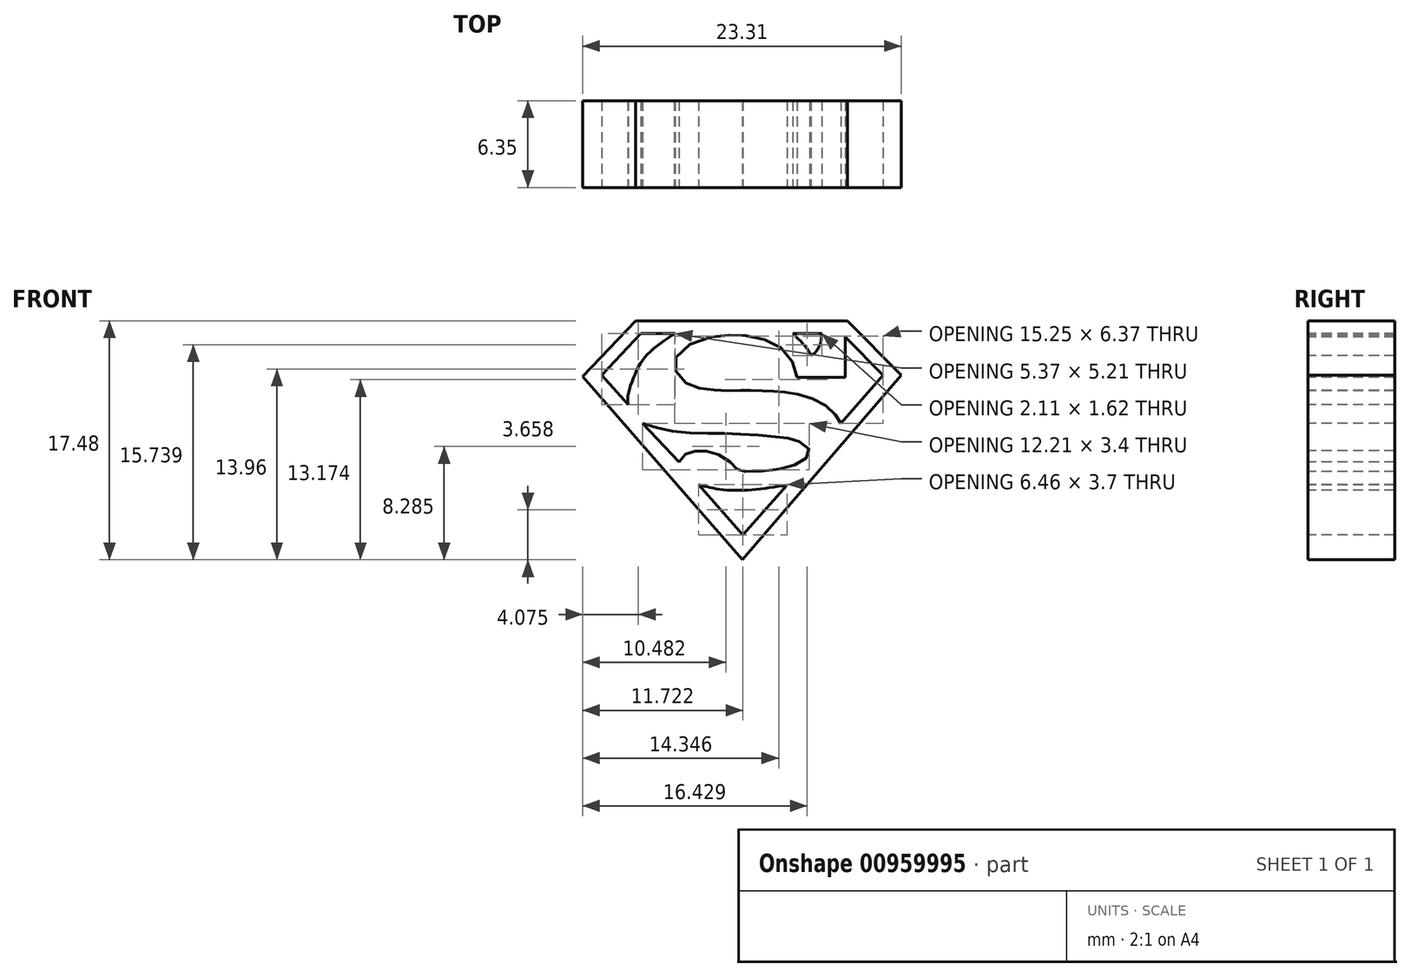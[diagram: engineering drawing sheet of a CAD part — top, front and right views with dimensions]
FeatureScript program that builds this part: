
annotation { "Feature Type Name" : "Feature", "Feature Type Description" : "" }
export const myFeature = defineFeature(function(context is Context, id is Id, definition is map)
    precondition{}
    {
        {
            var Q0;
            Q0=qCreatedBy(makeId("Front.planeOp"),FACE);
            var sketch = newSketch(context, id + "F0", { "sketchPlane" : qUnion([Q0])});
            skLineSegment(sketch, "E0", {"start": v(0, 0) * mm, "end": v(0, 25.4) * mm});
            skLineSegment(sketch, "E1", {"start": v(0, 25.4) * mm, "end": v(25.4, 25.4) * mm});
            skLineSegment(sketch, "E2", {"start": v(25.4, 25.4) * mm, "end": v(25.4, 0) * mm});
            skLineSegment(sketch, "E3", {"start": v(25.4, 0) * mm, "end": v(0, 0) * mm});
            skSolve(sketch);
        }
        {
            var Q0;
            Q0=qSketchRegion(id+"F0",true);
            extrude(context, id + "F1", {"entities" : qUnion([Q0]), "depth" : 6.35 * mm, "offsetDistance" : 25.4 * mm});
        }
        {
            var Q0;
            Q0=makeQuery(id+"F1.opExtrude","CAP_FACE",FACE,{"disambiguationData":[OSD([sQuery(id+"F0.wireOp",EDGE,"E0"),sQuery(id+"F0.wireOp",EDGE,"E1"),sQuery(id+"F0.wireOp",EDGE,"E2"),sQuery(id+"F0.wireOp",EDGE,"E3")])],"isStart":false});
            var sketch = newSketch(context, id + "F2", { "sketchPlane" : qUnion([Q0])});
            skLineSegment(sketch, "E4", {"start": v(4.73, 18.97) * mm, "end": v(20.63, 18.97) * mm});
            skLineSegment(sketch, "E5", {"start": v(20.63, 18.97) * mm, "end": v(24.95, 14.54) * mm});
            skLineSegment(sketch, "E6", {"start": v(24.95, 14.54) * mm, "end": v(12.72, 0.33) * mm});
            skLineSegment(sketch, "E7", {"start": v(12.72, 0.33) * mm, "end": v(0.33, 14.54) * mm});
            skFitSpline(sketch, "E8", {"points": [v(8.08, 8.2) * mm, v(8.73, 8.85) * mm, v(9.74, 9) * mm, v(11.07, 8.68) * mm, v(12.24, 7.8) * mm, v(12.48, 7.56) * mm, v(14.74, 7.6) * mm, v(16.88, 8.12) * mm, v(17.64, 9) * mm, v(16.68, 9.77) * mm, v(15.47, 10.02) * mm, v(12.84, 10.22) * mm, v(10.38, 10.3) * mm, v(7.52, 10.46) * mm, v(5.42, 11.03) * mm], "startDerivative": vector(10.55, 13.9) * mm, "endDerivative": vector(-23.62, 7.93) * mm});
            skLineSegment(sketch, "E9", {"start": v(5.42, 11.03) * mm, "end": v(8.08, 8.2) * mm});
            skLineSegment(sketch, "E10", {"start": v(4.37, 12.4) * mm, "end": v(2.43, 14.54) * mm});
            skLineSegment(sketch, "E11", {"start": v(2.43, 14.54) * mm, "end": v(5.3, 17.6) * mm});
            skLineSegment(sketch, "E12", {"start": v(5.3, 17.6) * mm, "end": v(7.8, 17.6) * mm});
            skFitSpline(sketch, "E13", {"points": [v(4.37, 12.4) * mm, v(4.37, 13.12) * mm, v(4.77, 14.37) * mm, v(5.38, 15.58) * mm, v(6.39, 16.6) * mm, v(7.8, 17.6) * mm], "startDerivative": vector(-0.43, 4.52) * mm, "endDerivative": vector(6.31, 4.29) * mm});
            skLineSegment(sketch, "E14", {"start": v(9.53, 6.55) * mm, "end": v(12.76, 2.85) * mm});
            skLineSegment(sketch, "E15", {"start": v(12.76, 2.85) * mm, "end": v(15.99, 6.5) * mm});
            skFitSpline(sketch, "E16", {"points": [v(9.53, 6.55) * mm, v(10.87, 6.22) * mm, v(13.12, 6.14) * mm, v(15.99, 6.5) * mm], "startDerivative": vector(4.65, -1.37) * mm, "endDerivative": vector(7.47, 1.19) * mm});
            skLineSegment(sketch, "E17", {"start": v(16.41, 17.59) * mm, "end": v(18.52, 17.59) * mm});
            skFitSpline(sketch, "E18", {"points": [v(16.41, 17.59) * mm, v(16.56, 17.46) * mm, v(16.75, 17.27) * mm, v(17.05, 16.97) * mm, v(17.36, 16.6) * mm, v(17.62, 16.24) * mm, v(17.74, 15.97) * mm], "startDerivative": vector(1.14, -0.95) * mm, "endDerivative": vector(0.64, -1.7) * mm});
            skFitSpline(sketch, "E19", {"points": [v(17.74, 15.97) * mm, v(17.84, 16.03) * mm, v(17.98, 16.13) * mm, v(18.13, 16.3) * mm, v(18.3, 16.56) * mm, v(18.44, 16.88) * mm, v(18.5, 17.32) * mm, v(18.52, 17.59) * mm], "startDerivative": vector(1, 0.53) * mm, "endDerivative": vector(0.07, 1.68) * mm});
            skLineSegment(sketch, "E20", {"start": v(16.72, 14.39) * mm, "end": v(20.25, 14.39) * mm});
            skLineSegment(sketch, "E21", {"start": v(20.25, 14.39) * mm, "end": v(20.25, 17.35) * mm});
            skLineSegment(sketch, "E22", {"start": v(20.25, 17.35) * mm, "end": v(23.01, 14.54) * mm});
            skLineSegment(sketch, "E23", {"start": v(23.01, 14.54) * mm, "end": v(19.92, 11.03) * mm});
            skFitSpline(sketch, "E24", {"points": [v(19.92, 11.03) * mm, v(19.82, 11.26) * mm, v(19.62, 11.54) * mm, v(19.36, 11.85) * mm, v(18.98, 12.22) * mm, v(18.2, 12.68) * mm, v(17.79, 12.86) * mm, v(17.13, 13.07) * mm, v(16.54, 13.2) * mm, v(16.01, 13.3) * mm, v(15.45, 13.35) * mm, v(15.2, 13.38) * mm, v(14.8, 13.39) * mm, v(14.44, 13.4) * mm, v(14.04, 13.42) * mm, v(13.6, 13.43) * mm, v(13.28, 13.42) * mm, v(13, 13.42) * mm, v(12.68, 13.42) * mm, v(12.36, 13.42) * mm, v(11.75, 13.41) * mm, v(11.14, 13.42) * mm, v(10.6, 13.46) * mm, v(9.96, 13.53) * mm, v(9.31, 13.68) * mm, v(8.7, 13.92) * mm, v(8.15, 14.34) * mm, v(7.82, 14.95) * mm, v(7.76, 15.53) * mm, v(8.14, 16.27) * mm, v(9.33, 17) * mm, v(10.7, 17.38) * mm, v(11.67, 17.47) * mm, v(12.51, 17.46) * mm, v(13.4, 17.37) * mm, v(14.48, 17.11) * mm, v(15.44, 16.61) * mm, v(16.1, 15.98) * mm, v(16.58, 15.09) * mm, v(16.72, 14.39) * mm], "startDerivative": vector(-5.38, 14) * mm, "endDerivative": vector(3.46, -24.46) * mm});
            skLineSegment(sketch, "E25", {"start": v(0.33, 14.54) * mm, "end": v(4.73, 18.97) * mm});
            skLineSegment(sketch, "E26", {"start": v(4.92, 18.52) * mm, "end": v(20.42, 18.52) * mm});
            skLineSegment(sketch, "E27", {"start": v(20.42, 18.52) * mm, "end": v(24.35, 14.53) * mm});
            skLineSegment(sketch, "E28", {"start": v(24.35, 14.53) * mm, "end": v(12.74, 1.04) * mm});
            skLineSegment(sketch, "E29", {"start": v(12.74, 1.04) * mm, "end": v(1.04, 14.46) * mm});
            skLineSegment(sketch, "E30", {"start": v(1.04, 14.46) * mm, "end": v(4.92, 18.52) * mm});
            skSolve(sketch);
        }
        {
            var Q0;
            Q0=makeQuery(id+"F2.imprint","IMPRINT",FACE,{"disambiguationData":[TD([[makeQuery(id+"F2.imprint","IMPRINT",EDGE,{"derivedFrom":sQuery(id+"F2.wireOp",EDGE,"E10")}),-1.0]])]});
            var Q1;
            Q1=makeQuery(id+"F2.imprint","IMPRINT",FACE,{"disambiguationData":[TD([[makeQuery(id+"F2.imprint","IMPRINT",EDGE,{"derivedFrom":sQuery(id+"F2.wireOp",EDGE,"E20")}),-1.0]])]});
            var Q2;
            Q2=makeQuery(id+"F2.imprint","IMPRINT",FACE,{"disambiguationData":[TD([[makeQuery(id+"F2.imprint","IMPRINT",EDGE,{"derivedFrom":sQuery(id+"F2.wireOp",EDGE,"E17")}),-1.0]])]});
            var Q3;
            Q3=makeQuery(id+"F2.imprint","IMPRINT",FACE,{"disambiguationData":[TD([[makeQuery(id+"F2.imprint","IMPRINT",EDGE,{"derivedFrom":sQuery(id+"F2.wireOp",EDGE,"E8")}),1.0]])]});
            var Q4;
            Q4=makeQuery(id+"F2.imprint","IMPRINT",FACE,{"disambiguationData":[TD([[makeQuery(id+"F2.imprint","IMPRINT",EDGE,{"derivedFrom":sQuery(id+"F2.wireOp",EDGE,"E14")}),1.0]])]});
            var Q5;
            Q5=makeQuery(id+"F2.imprint","IMPRINT",FACE,{"disambiguationData":[TD([[makeQuery(id+"F2.imprint","IMPRINT",EDGE,{"derivedFrom":sQuery(id+"F2.wireOp",EDGE,"E4")}),-1.0]])]});
            var Q6;
            Q6=makeQuery(id+"F2.imprint","IMPRINT",FACE,{"disambiguationData":[TD([[makeQuery(id+"F2.imprint","IMPRINT",EDGE,{"derivedFrom":sQuery(id+"F2.wireOp",EDGE,"E4")}),1.0]])]});
            extrude(context, id + "F3", {"entities" : qUnion([Q0, Q1, Q2, Q3, Q4, Q5, Q6]), "operationType" : NewBodyOperationType.REMOVE, "oppositeDirection" : true, "depth" : 25.4 * mm, "offsetDistance" : 25.4 * mm});
        }
    });
